# Revit family: QF_Vollrath_40732
name_source: partatom
category: Specialty Equipment
revit_build: Autodesk Revit 2018 (Build: 20190510_1515(x64)
units: mm (PartAtom-declared; Revit-internal decimal feet)

## family parameters
Always vertical = Yes
Cut with Voids When Loaded = No
OmniClass Number = 23.40.40.11.21
OmniClass Title = Hot Cabinets
Part Type = Normal
Room Calculation Point = No
Round Connector Dimension = Use Diameter
Shared = No
Work Plane-Based = No

## types (1)
- 40732/BMA7103
    Apparent Power = 1440 VA
    Assembly Code = E1090320
    CSI MasterFormat = 11 41 00
    Conn Plug = NEMA 5-15P
    Cycle = 60 Hz
    Description = Bain Marie Display Case
    FL Amps = 12 A
    Manufacturer = Vollrath
    Model = 40732/BMA7103
    Phase = 1
    URL = www.vollrathfoodservice.com
    Volts = 120 V
    Watts = 1440 W
    Weight in Pounds = 143
    Width = 3' - 6"

## geometry (parser evidence)
native form markers: Blend x10, Sweep x4
no freeform markers — native parametric forms only
